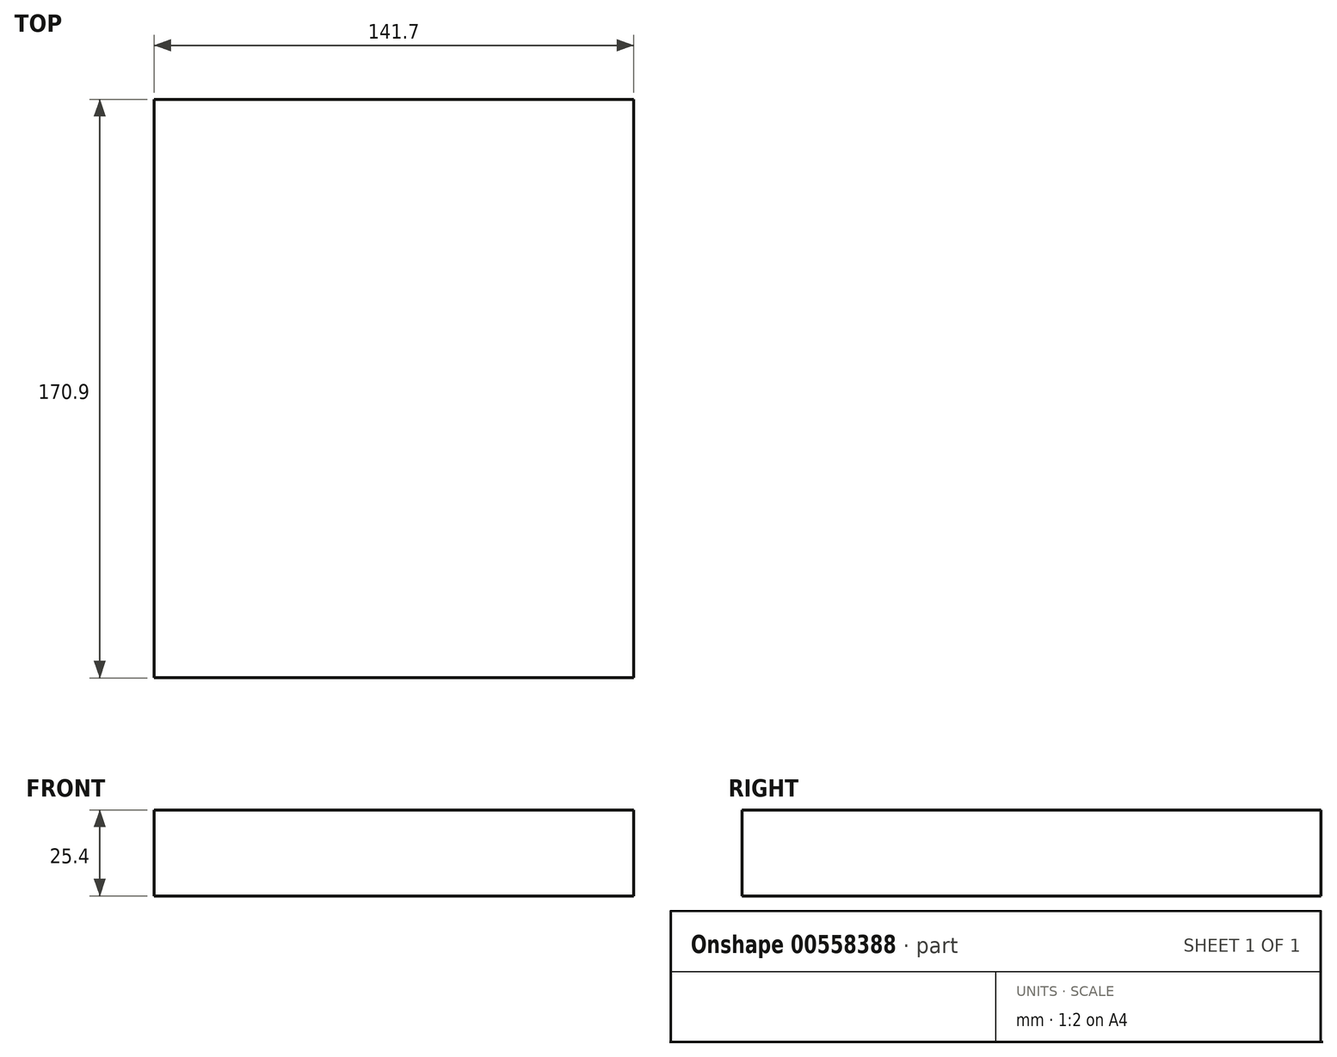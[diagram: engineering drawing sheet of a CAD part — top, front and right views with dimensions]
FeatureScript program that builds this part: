
annotation { "Feature Type Name" : "Feature", "Feature Type Description" : "" }
export const myFeature = defineFeature(function(context is Context, id is Id, definition is map)
    precondition{}
    {
        {
            var Q0;
            Q0=qCreatedBy(makeId("Top.planeOp"),FACE);
            var sketch = newSketch(context, id + "F0", { "sketchPlane" : qUnion([Q0])});
            skLineSegment(sketch, "E0.bottom", {"start": v(-70.85, -85.45) * mm, "end": v(70.85, -85.45) * mm});
            skLineSegment(sketch, "E0.top", {"start": v(-70.85, 85.45) * mm, "end": v(70.85, 85.45) * mm});
            skLineSegment(sketch, "E0.left", {"start": v(-70.85, -85.45) * mm, "end": v(-70.85, 85.45) * mm});
            skLineSegment(sketch, "E0.right", {"start": v(70.85, -85.45) * mm, "end": v(70.85, 85.45) * mm});
            skPoint(sketch, "E0.middle", {"position": v(0, 0) * mm});
            skSolve(sketch);
        }
        {
            var Q0;
            Q0=makeQuery(id+"F0.imprint","IMPRINT",FACE,{"disambiguationData":[TD([[makeQuery(id+"F0.imprint","IMPRINT",EDGE,{"derivedFrom":sQuery(id+"F0.wireOp",EDGE,"E0.bottom")}),1.0]])]});
            extrude(context, id + "F1", {"entities" : qUnion([Q0]), "depth" : 25.4 * mm, "offsetDistance" : 25.4 * mm});
        }
    });
